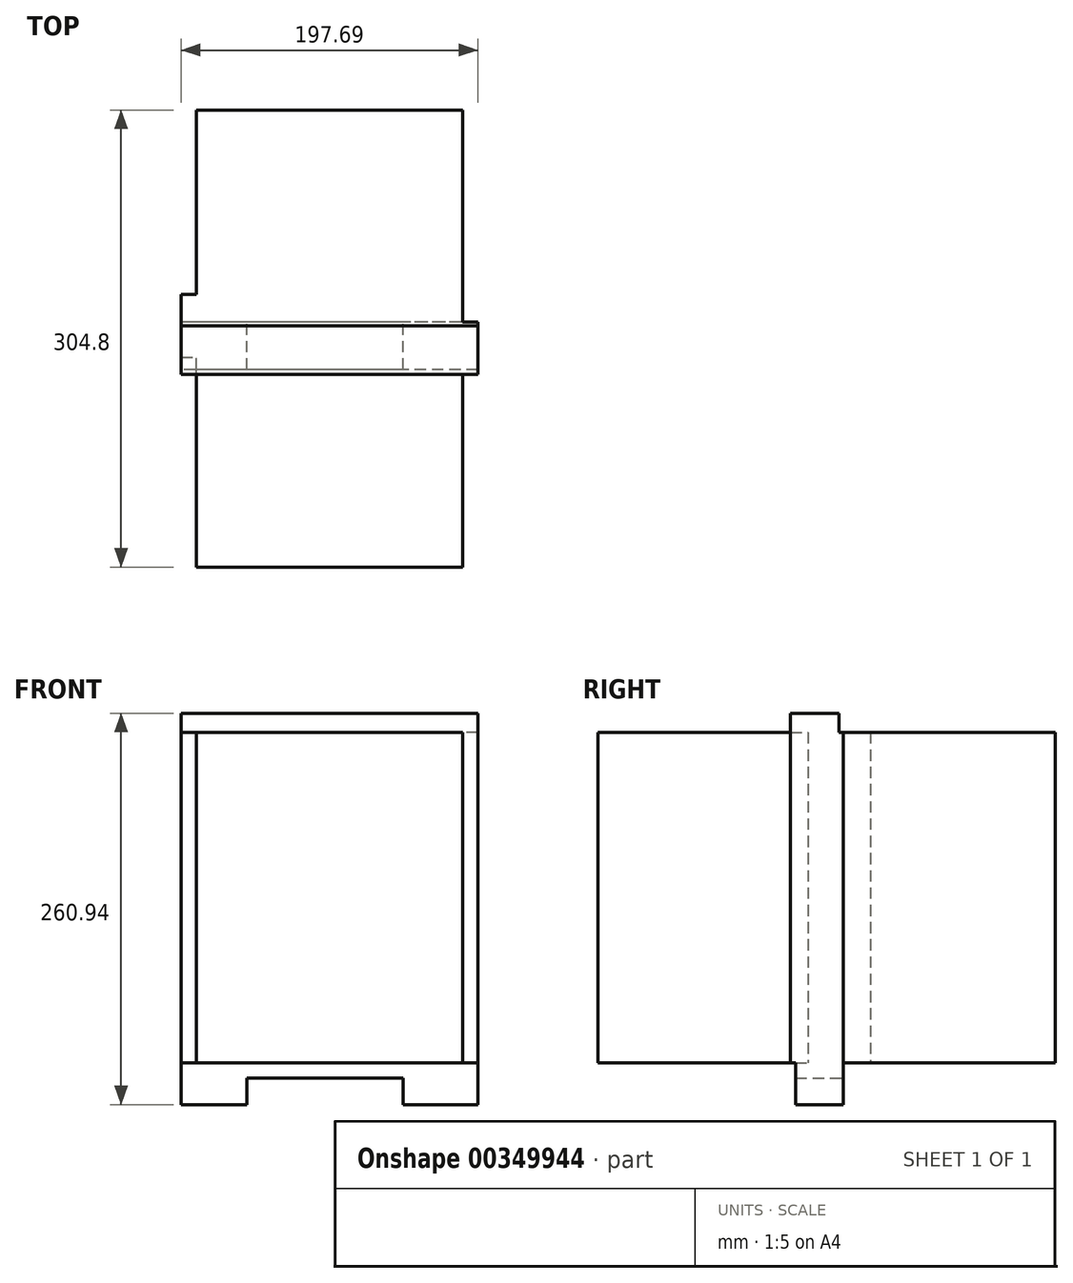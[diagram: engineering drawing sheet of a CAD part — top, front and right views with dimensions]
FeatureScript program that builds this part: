
annotation { "Feature Type Name" : "Feature", "Feature Type Description" : "" }
export const myFeature = defineFeature(function(context is Context, id is Id, definition is map)
    precondition{}
    {
        {
            var Q0;
            Q0=qCreatedBy(makeId("Front.planeOp"),FACE);
            var sketch = newSketch(context, id + "F0", { "sketchPlane" : qUnion([Q0])});
            skLineSegment(sketch, "E0.bottom", {"start": v(-87.84, 153.97) * mm, "end": v(89.53, 153.97) * mm});
            skLineSegment(sketch, "E0.top", {"start": v(-87.84, -66.33) * mm, "end": v(89.53, -66.33) * mm});
            skLineSegment(sketch, "E0.left", {"start": v(-87.84, 153.97) * mm, "end": v(-87.84, -66.33) * mm});
            skLineSegment(sketch, "E0.right", {"start": v(89.53, 153.97) * mm, "end": v(89.53, -66.33) * mm});
            skSolve(sketch);
        }
        {
            var Q0;
            Q0 = qSketchRegion(id + "F0", true);
            extrude(context, id + "F1", {"entities" : qUnion([Q0]), "depth" : 304.8 * mm, "offsetDistance" : 25.4 * mm});
        }
        {
            var Q0;
            Q0=makeQuery(id+"F1.opExtrude","SWEPT_FACE",FACE,{"disambiguationData":[OSD([sQuery(id+"F0.wireOp",EDGE,"E0.left")])]});
            var sketch = newSketch(context, id + "F2", { "sketchPlane" : qUnion([Q0])});
            skLineSegment(sketch, "E1.bottom", {"start": v(123.11, 153.97) * mm, "end": v(164.85, 153.97) * mm});
            skLineSegment(sketch, "E1.top", {"start": v(123.11, -66.33) * mm, "end": v(164.85, -66.33) * mm});
            skLineSegment(sketch, "E1.left", {"start": v(123.11, 153.97) * mm, "end": v(123.11, -66.33) * mm});
            skLineSegment(sketch, "E1.right", {"start": v(164.85, 153.97) * mm, "end": v(164.85, -66.33) * mm});
            skSolve(sketch);
        }
        {
            var Q0;
            Q0 = qSketchRegion(id + "F2", true);
            extrude(context, id + "F3", {"entities" : qUnion([Q0]), "operationType" : NewBodyOperationType.ADD, "depth" : 10.16 * mm, "offsetDistance" : 25.4 * mm});
        }
        {
            var Q0;
            Q0=makeQuery(id+"F1.opExtrude","SWEPT_FACE",FACE,{"disambiguationData":[OSD([sQuery(id+"F0.wireOp",EDGE,"E0.right")])]});
            var sketch = newSketch(context, id + "F4", { "sketchPlane" : qUnion([Q0])});
            skLineSegment(sketch, "E2.bottom", {"start": v(-176.4, 153.97) * mm, "end": v(-141.34, 153.97) * mm});
            skLineSegment(sketch, "E2.top", {"start": v(-176.4, -66.33) * mm, "end": v(-141.34, -66.33) * mm});
            skLineSegment(sketch, "E2.left", {"start": v(-176.4, 153.97) * mm, "end": v(-176.4, -66.33) * mm});
            skLineSegment(sketch, "E2.right", {"start": v(-141.34, 153.97) * mm, "end": v(-141.34, -66.33) * mm});
            skSolve(sketch);
        }
        {
            var Q0;
            Q0 = qSketchRegion(id + "F4", true);
            extrude(context, id + "F5", {"entities" : qUnion([Q0]), "operationType" : NewBodyOperationType.ADD, "depth" : 10.16 * mm, "offsetDistance" : 25.4 * mm});
        }
        {
            var Q0;
            Q0=makeQuery(id+"F5.boolean.opBoolean","MERGE",FACE,{"derivedFrom":[makeQuery(id+"F3.boolean.opBoolean","MERGE",FACE,{"derivedFrom":[makeQuery(id+"F1.opExtrude","SWEPT_FACE",FACE,{"disambiguationData":[OSD([sQuery(id+"F0.wireOp",EDGE,"E0.top")])]}),makeQuery(id+"F3.opExtrude","SWEPT_FACE",FACE,{"disambiguationData":[OSD([sQuery(id+"F2.wireOp",EDGE,"E1.top")])]})]}),makeQuery(id+"F5.opExtrude","SWEPT_FACE",FACE,{"disambiguationData":[OSD([sQuery(id+"F4.wireOp",EDGE,"E2.top")])]})]});
            var sketch = newSketch(context, id + "F6", { "sketchPlane" : qUnion([Q0])});
            skLineSegment(sketch, "E3.bottom", {"start": v(99.69, 141.34) * mm, "end": v(-98, 141.34) * mm});
            skLineSegment(sketch, "E3.top", {"start": v(99.69, 173.03) * mm, "end": v(-98, 173.03) * mm});
            skLineSegment(sketch, "E3.left", {"start": v(99.69, 141.34) * mm, "end": v(99.69, 173.03) * mm});
            skLineSegment(sketch, "E3.right", {"start": v(-98, 141.34) * mm, "end": v(-98, 173.03) * mm});
            skSolve(sketch);
        }
        {
            var Q0;
            Q0 = qSketchRegion(id + "F6", true);
            extrude(context, id + "F7", {"entities" : qUnion([Q0]), "operationType" : NewBodyOperationType.ADD, "depth" : 10.16 * mm, "offsetDistance" : 25.4 * mm});
        }
        {
            var Q0;
            Q0=makeQuery(id+"F5.boolean.opBoolean","MERGE",FACE,{"derivedFrom":[makeQuery(id+"F3.boolean.opBoolean","MERGE",FACE,{"derivedFrom":[makeQuery(id+"F1.opExtrude","SWEPT_FACE",FACE,{"disambiguationData":[OSD([sQuery(id+"F0.wireOp",EDGE,"E0.bottom")])]}),makeQuery(id+"F3.opExtrude","SWEPT_FACE",FACE,{"disambiguationData":[OSD([sQuery(id+"F2.wireOp",EDGE,"E1.bottom")])]})]}),makeQuery(id+"F5.opExtrude","SWEPT_FACE",FACE,{"disambiguationData":[OSD([sQuery(id+"F4.wireOp",EDGE,"E2.bottom")])]})]});
            var sketch = newSketch(context, id + "F8", { "sketchPlane" : qUnion([Q0])});
            skLineSegment(sketch, "E4.bottom", {"start": v(99.69, -176.4) * mm, "end": v(-98, -176.4) * mm});
            skLineSegment(sketch, "E4.top", {"start": v(99.69, -143.98) * mm, "end": v(-98, -143.98) * mm});
            skLineSegment(sketch, "E4.left", {"start": v(99.69, -176.4) * mm, "end": v(99.69, -143.98) * mm});
            skLineSegment(sketch, "E4.right", {"start": v(-98, -176.4) * mm, "end": v(-98, -143.98) * mm});
            skSolve(sketch);
        }
        {
            var Q0;
            Q0 = qSketchRegion(id + "F8", true);
            extrude(context, id + "F9", {"entities" : qUnion([Q0]), "operationType" : NewBodyOperationType.ADD, "depth" : 12.7 * mm, "offsetDistance" : 25.4 * mm});
        }
        {
            var Q0;
            Q0=makeQuery(id+"F7.opExtrude","CAP_FACE",FACE,{"disambiguationData":[OSD([sQuery(id+"F6.wireOp",EDGE,"E3.bottom"),sQuery(id+"F6.wireOp",EDGE,"E3.top"),sQuery(id+"F6.wireOp",EDGE,"E3.left"),sQuery(id+"F6.wireOp",EDGE,"E3.right")])],"isStart":false});
            var sketch = newSketch(context, id + "F10", { "sketchPlane" : qUnion([Q0])});
            skLineSegment(sketch, "E5.bottom", {"start": v(-98, 173.03) * mm, "end": v(-54.26, 173.03) * mm});
            skLineSegment(sketch, "E5.top", {"start": v(-98, 141.34) * mm, "end": v(-54.26, 141.34) * mm});
            skLineSegment(sketch, "E5.left", {"start": v(-98, 173.03) * mm, "end": v(-98, 141.34) * mm});
            skLineSegment(sketch, "E5.right", {"start": v(-54.26, 173.03) * mm, "end": v(-54.26, 141.34) * mm});
            skLineSegment(sketch, "E6.bottom", {"start": v(99.69, 173.03) * mm, "end": v(49.77, 173.03) * mm});
            skLineSegment(sketch, "E6.top", {"start": v(99.69, 141.34) * mm, "end": v(49.77, 141.34) * mm});
            skLineSegment(sketch, "E6.left", {"start": v(99.69, 173.03) * mm, "end": v(99.69, 141.34) * mm});
            skLineSegment(sketch, "E6.right", {"start": v(49.77, 173.03) * mm, "end": v(49.77, 141.34) * mm});
            skSolve(sketch);
        }
        {
            var Q0;
            Q0 = qSketchRegion(id + "F10", true);
            extrude(context, id + "F11", {"entities" : qUnion([Q0]), "operationType" : NewBodyOperationType.ADD, "depth" : 17.78 * mm, "offsetDistance" : 25.4 * mm});
        }
    });
